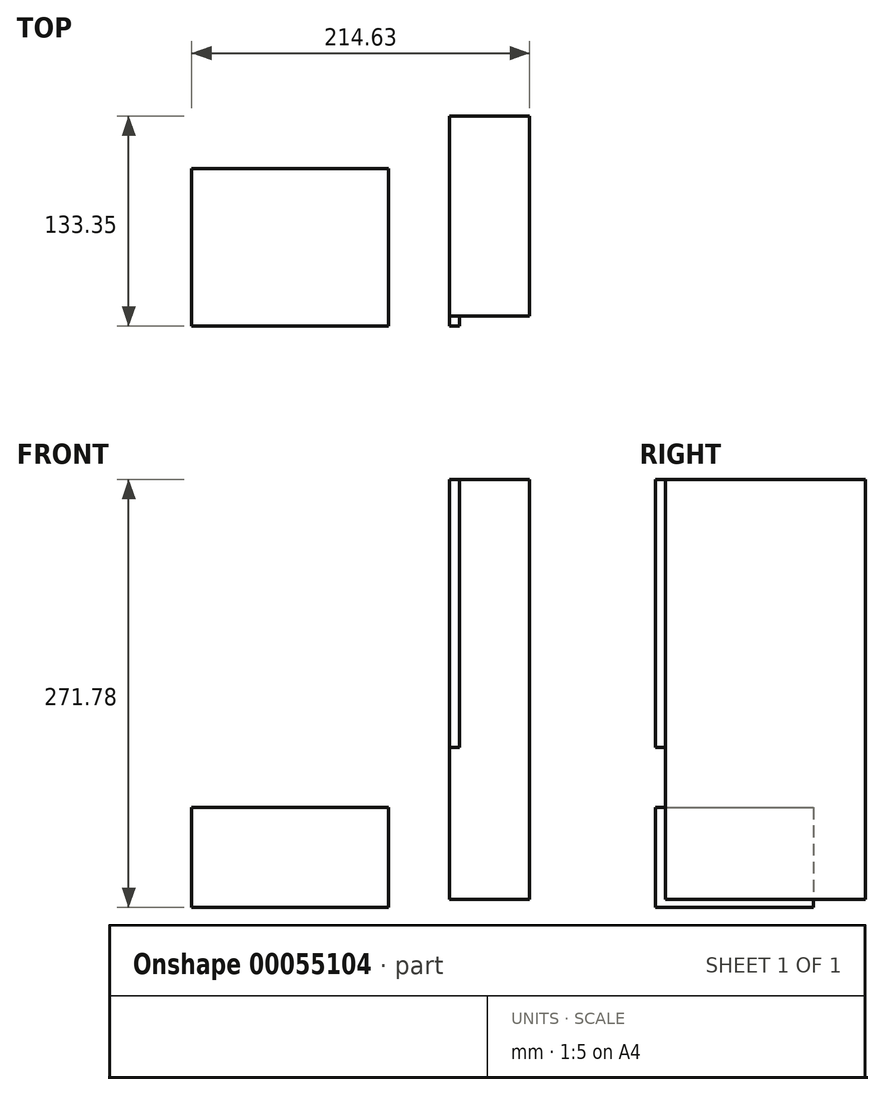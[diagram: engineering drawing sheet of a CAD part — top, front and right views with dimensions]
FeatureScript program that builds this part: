
annotation { "Feature Type Name" : "Feature", "Feature Type Description" : "" }
export const myFeature = defineFeature(function(context is Context, id is Id, definition is map)
    precondition{}
    {
        {
            var Q0;
            Q0=qCreatedBy(makeId("Top.planeOp"),FACE);
            var sketch = newSketch(context, id + "F0", { "sketchPlane" : qUnion([Q0])});
            skLineSegment(sketch, "E0.bottom", {"start": v(0, 0) * mm, "end": v(124.97, 0) * mm});
            skLineSegment(sketch, "E0.top", {"start": v(0, 100.08) * mm, "end": v(124.97, 100.08) * mm});
            skLineSegment(sketch, "E0.left", {"start": v(0, 0) * mm, "end": v(0, 100.08) * mm});
            skLineSegment(sketch, "E0.right", {"start": v(124.97, 0) * mm, "end": v(124.97, 100.08) * mm});
            skSolve(sketch);
        }
        {
            var Q0;
            Q0=makeQuery(id+"F0.imprint","IMPRINT",FACE,{"disambiguationData":[TD([[makeQuery(id+"F0.imprint","IMPRINT",EDGE,{"derivedFrom":sQuery(id+"F0.wireOp",EDGE,"E0.bottom")}),1.0]])]});
            extrude(context, id + "F1", {"entities" : qUnion([Q0]), "depth" : 63.5 * mm});
        }
        {
            var Q0;
            Q0=makeQuery(id+"F1.opExtrude","SWEPT_FACE",FACE,{"disambiguationData":[OSD([sQuery(id+"F0.wireOp",EDGE,"E0.bottom")])]});
            var sketch = newSketch(context, id + "F2", { "sketchPlane" : qUnion([Q0])});
            skLineSegment(sketch, "E1.0", {"start": v(0, 63.5) * mm, "end": v(124.97, 63.5) * mm});
            skLineSegment(sketch, "E2.0", {"start": v(0, 101.6) * mm, "end": v(124.97, 101.6) * mm});
            skLineSegment(sketch, "E3.bottom", {"start": v(0, 101.6) * mm, "end": v(170.18, 101.6) * mm});
            skLineSegment(sketch, "E3.top", {"start": v(0, 271.78) * mm, "end": v(170.18, 271.78) * mm});
            skLineSegment(sketch, "E3.left", {"start": v(0, 101.6) * mm, "end": v(0, 271.78) * mm});
            skLineSegment(sketch, "E3.right", {"start": v(170.18, 101.6) * mm, "end": v(170.18, 271.78) * mm});
            skLineSegment(sketch, "E4.0", {"start": v(163.83, 101.6) * mm, "end": v(163.83, 271.78) * mm, "construction": true});
            skLineSegment(sketch, "E5.bottom", {"start": v(163.83, 271.78) * mm, "end": v(214.63, 271.78) * mm});
            skLineSegment(sketch, "E5.top", {"start": v(163.83, 5.08) * mm, "end": v(214.63, 5.08) * mm});
            skLineSegment(sketch, "E5.left", {"start": v(163.83, 271.78) * mm, "end": v(163.83, 5.08) * mm});
            skLineSegment(sketch, "E5.right", {"start": v(214.63, 271.78) * mm, "end": v(214.63, 5.08) * mm});
            skSolve(sketch);
        }
        {
            var Q0;
            {var subQ4=sQuery(id+"F2.wireOp",EDGE,"E3.top");Q0=makeQuery(id+"F2.imprint","IMPRINT",FACE,{"disambiguationData":[TD([[makeQuery(id+"F2.imprint","IMPRINT",EDGE,{"derivedFrom":subQ4}),-1.0]])]});}
            var Q1;
            {var subQ0=sQuery(id+"F2.wireOp",EDGE,"E3.right");Q1=makeQuery(id+"F2.imprint","IMPRINT",FACE,{"disambiguationData":[TD([[makeQuery(id+"F2.imprint","IMPRINT",EDGE,{"derivedFrom":subQ0}),1.0]])]});}
            extrude(context, id + "F3", {"entities" : qUnion([Q0, Q1]), "oppositeDirection" : true, "depth" : 6.35 * mm});
        }
        {
            var Q0;
            Q0=makeQuery(id+"F3.opExtrude","CAP_FACE",FACE,{"disambiguationData":[OSD([sQuery(id+"F2.wireOp",EDGE,"E3.bottom"),sQuery(id+"F2.wireOp",EDGE,"E3.top"),sQuery(id+"F2.wireOp",EDGE,"E3.left"),sQuery(id+"F2.wireOp",EDGE,"E3.right"),sQuery(id+"F2.wireOp",EDGE,"E5.bottom")])],"isStart":false});
            var sketch = newSketch(context, id + "F4", { "sketchPlane" : qUnion([Q0])});
            skLineSegment(sketch, "E6.0.0", {"start": v(-170.18, 101.6) * mm, "end": v(-163.83, 101.6) * mm});
            skLineSegment(sketch, "E6.0.1", {"start": v(-163.83, 101.6) * mm, "end": v(-163.83, 5.08) * mm});
            skLineSegment(sketch, "E6.0.2", {"start": v(-163.83, 5.08) * mm, "end": v(-214.63, 5.08) * mm});
            skLineSegment(sketch, "E6.0.3", {"start": v(-214.63, 5.08) * mm, "end": v(-214.63, 271.78) * mm});
            skLineSegment(sketch, "E6.0.4", {"start": v(-214.63, 271.78) * mm, "end": v(-170.18, 271.78) * mm});
            skLineSegment(sketch, "E6.0.5", {"start": v(-170.18, 271.78) * mm, "end": v(-170.18, 101.6) * mm});
            skLineSegment(sketch, "E7.bottom", {"start": v(-214.63, 5.08) * mm, "end": v(-163.83, 5.08) * mm});
            skLineSegment(sketch, "E7.top", {"start": v(-214.63, 271.78) * mm, "end": v(-163.83, 271.78) * mm});
            skLineSegment(sketch, "E7.right", {"start": v(-163.83, 5.08) * mm, "end": v(-163.83, 271.78) * mm});
            skSolve(sketch);
        }
        {
            var Q0;
            {var subQ4=sQuery(id+"F4.wireOp",EDGE,"E6.0.0");Q0=makeQuery(id+"F4.imprint","IMPRINT",FACE,{"disambiguationData":[TD([[makeQuery(id+"F4.imprint","IMPRINT",EDGE,{"derivedFrom":subQ4}),1.0]])]});}
            var Q1;
            {var subQ0=sQuery(id+"F4.wireOp",EDGE,"E6.0.0");Q1=makeQuery(id+"F4.imprint","IMPRINT",FACE,{"disambiguationData":[TD([[makeQuery(id+"F4.imprint","IMPRINT",EDGE,{"derivedFrom":subQ0}),-1.0]])]});}
            extrude(context, id + "F5", {"entities" : qUnion([Q0, Q1]), "depth" : 127 * mm});
        }
    });
